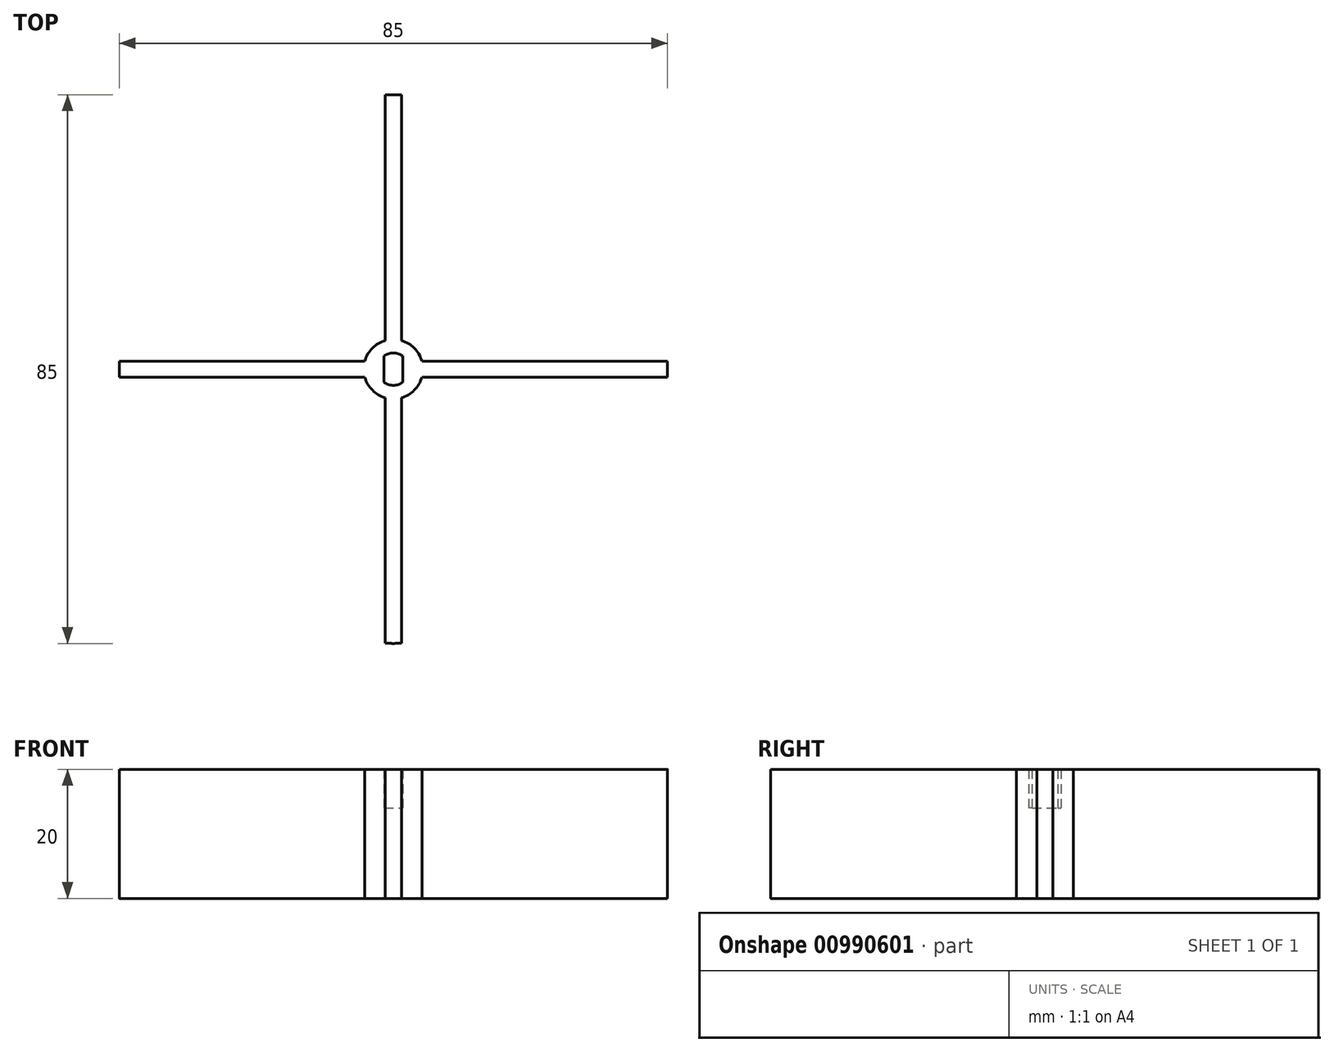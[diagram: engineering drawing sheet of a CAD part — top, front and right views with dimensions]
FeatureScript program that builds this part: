
annotation { "Feature Type Name" : "Feature", "Feature Type Description" : "" }
export const myFeature = defineFeature(function(context is Context, id is Id, definition is map)
    precondition{}
    {
        {
            var Q0;
            Q0=qCreatedBy(makeId("Top.planeOp"),FACE);
            var sketch = newSketch(context, id + "F0", { "sketchPlane" : qUnion([Q0])});
            skCircle(sketch, "E0", {"center": v(0, 0) * mm, "radius": 2.5 * mm});
            skSolve(sketch);
        }
        {
            var Q0;
            Q0 = qSketchRegion(id + "F0", true);
            extrude(context, id + "F1", {"entities" : qUnion([Q0]), "depth" : 8 * mm, "offsetDistance" : 25 * mm});
        }
        {
            var Q0;
            Q0=makeQuery(id+"F1.opExtrude","CAP_FACE",FACE,{"disambiguationData":[OSD([sQuery(id+"F0.wireOp",EDGE,"E0")])],"isStart":true});
            var sketch = newSketch(context, id + "F2", { "sketchPlane" : qUnion([Q0])});
            skLineSegment(sketch, "E1", {"start": v(-1.47, 2.02) * mm, "end": v(-1.48, -2.02) * mm});
            skLineSegment(sketch, "E2", {"start": v(1.48, 2.02) * mm, "end": v(1.47, -2.02) * mm});
            skLineSegment(sketch, "E3", {"start": v(-1.48, 0) * mm, "end": v(1.48, 0) * mm, "construction": true});
            skArc(sketch, "E4.0", {"start": v(-1.47, 2.02) * mm, "mid": v(-2.5, 0) * mm, "end": v(-1.47, -2.02) * mm});
            skArc(sketch, "E5.trimOffspring", {"start": v(1.47, -2.02) * mm, "mid": v(2.5, 0) * mm, "end": v(1.47, 2.02) * mm});
            skSolve(sketch);
        }
        {
            var Q0;
            Q0 = qSketchRegion(id + "F2", true);
            extrude(context, id + "F3", {"entities" : qUnion([Q0]), "operationType" : NewBodyOperationType.REMOVE, "oppositeDirection" : true, "depth" : 6 * mm, "offsetDistance" : 25 * mm});
        }
        {
            var Q0;
            Q0=makeQuery(id+"F1.opExtrude","CAP_FACE",FACE,{"disambiguationData":[OSD([sQuery(id+"F0.wireOp",EDGE,"E0")])],"isStart":false});
            var sketch = newSketch(context, id + "F4", { "sketchPlane" : qUnion([Q0])});
            skCircle(sketch, "E6", {"center": v(0, 0) * mm, "radius": 4.6 * mm});
            skSolve(sketch);
        }
        {
            var Q0;
            Q0=makeQuery(id+"F4.imprint","IMPRINT",FACE,{"disambiguationData":[TD([[makeQuery(id+"F4.imprint","IMPRINT",EDGE,{"derivedFrom":sQuery(id+"F4.wireOp",EDGE,"E6")}),1.0]])]});
            var Q1;
            Q1=makeQuery(id+"F4.imprint","IMPRINT",FACE,{"disambiguationData":[TD([[makeQuery(id+"F4.imprint","IMPRINT",EDGE,{"derivedFrom":makeQuery(id+"F1.opExtrude","CAP_EDGE",EDGE,{"disambiguationData":[OSD([sQuery(id+"F0.wireOp",EDGE,"E0")])],"isStart":false})}),1.0]])]});
            extrude(context, id + "F5", {"entities" : qUnion([Q0, Q1]), "operationType" : NewBodyOperationType.ADD, "depth" : 1.5 * mm, "offsetDistance" : 25 * mm});
        }
        {
            var Q0;
            Q0=makeQuery(id+"F5.opExtrude","CAP_FACE",FACE,{"disambiguationData":[OSD([sQuery(id+"F4.wireOp",EDGE,"E6")])],"isStart":false});
            var sketch = newSketch(context, id + "F6", { "sketchPlane" : qUnion([Q0])});
            skCircle(sketch, "E7", {"center": v(0, 7.6) * mm, "radius": 14 * mm});
            skLineSegment(sketch, "E8", {"start": v(0, 0) * mm, "end": v(0, 7.6) * mm, "construction": true});
            skSolve(sketch);
        }
        {
            var Q0;
            Q0 = qSketchRegion(id + "F6", true);
            extrude(context, id + "F7", {"entities" : qUnion([Q0]), "operationType" : NewBodyOperationType.ADD, "depth" : 19.2 * mm, "offsetDistance" : 25 * mm});
        }
        {
            var Q0;
            Q0=makeQuery(id+"F7.opExtrude","CAP_FACE",FACE,{"disambiguationData":[OSD([sQuery(id+"F6.wireOp",EDGE,"E7")])],"isStart":true});
            var sketch = newSketch(context, id + "F8", { "sketchPlane" : qUnion([Q0])});
            skLineSegment(sketch, "E9", {"start": v(-7.25, -19.58) * mm, "end": v(-7.25, -24.08) * mm});
            skLineSegment(sketch, "E10", {"start": v(-7.25, -24.08) * mm, "end": v(7.25, -24.08) * mm});
            skLineSegment(sketch, "E11", {"start": v(7.25, -24.08) * mm, "end": v(7.25, -19.58) * mm});
            skLineSegment(sketch, "E12", {"start": v(0, 0) * mm, "end": v(0, -24.08) * mm, "construction": true});
            skLineSegment(sketch, "E13", {"start": v(-7.25, -19.58) * mm, "end": v(7.25, -19.58) * mm});
            skSolve(sketch);
        }
        {
            var Q0;
            {var subQ0=sQuery(id+"F8.wireOp",EDGE,"E9");Q0=makeQuery(id+"F8.imprint","IMPRINT",FACE,{"disambiguationData":[TD([[makeQuery(id+"F8.imprint","IMPRINT",EDGE,{"derivedFrom":subQ0}),1.0]])]});}
            extrude(context, id + "F9", {"entities" : qUnion([Q0]), "operationType" : NewBodyOperationType.ADD, "oppositeDirection" : true, "depth" : 16.5 * mm, "offsetDistance" : 25 * mm});
        }
        {
            var Q0;
            Q0=makeQuery(id+"F3.boolean.opBoolean","COPY",FACE,{"derivedFrom":makeQuery(id+"F3.opExtrude","CAP_FACE",FACE,{"disambiguationData":[OSD([sQuery(id+"F2.wireOp",EDGE,"E1"),sQuery(id+"F2.wireOp",EDGE,"E4.0")])],"isStart":false})});
            var sketch = newSketch(context, id + "F10", { "sketchPlane" : qUnion([Q0])});
            skArc(sketch, "E14", {"start": v(-1.25, -42.48) * mm, "mid": v(0, -42.5) * mm, "end": v(1.25, -42.48) * mm});
            skArc(sketch, "E15", {"start": v(-4.43, -1.25) * mm, "mid": v(-3.25, -3.25) * mm, "end": v(-1.25, -4.43) * mm});
            skLineSegment(sketch, "E16", {"start": v(1.25, 42.48) * mm, "end": v(1.25, 4.43) * mm});
            skLineSegment(sketch, "E17", {"start": v(0, 42.5) * mm, "end": v(0, -42.5) * mm, "construction": true});
            skLineSegment(sketch, "E18", {"start": v(42.5, 0) * mm, "end": v(-42.5, 0) * mm, "construction": true});
            skLineSegment(sketch, "E19", {"start": v(4.43, 1.25) * mm, "end": v(42.48, 1.25) * mm});
            skLineSegment(sketch, "E20", {"start": v(4.43, -1.25) * mm, "end": v(42.48, -1.25) * mm});
            skLineSegment(sketch, "E21", {"start": v(1.25, -4.43) * mm, "end": v(1.25, -42.48) * mm});
            skLineSegment(sketch, "E22.MirrorCS", {"start": v(-1.25, 42.48) * mm, "end": v(-1.25, 4.43) * mm});
            skLineSegment(sketch, "E23.MirrorCS", {"start": v(-4.43, 1.25) * mm, "end": v(-42.48, 1.25) * mm});
            skLineSegment(sketch, "E24.MirrorCS", {"start": v(-4.43, -1.25) * mm, "end": v(-42.48, -1.25) * mm});
            skLineSegment(sketch, "E25.MirrorCS", {"start": v(-1.25, -4.43) * mm, "end": v(-1.25, -42.48) * mm});
            skArc(sketch, "E26.trimOffspring", {"start": v(4.43, 1.25) * mm, "mid": v(3.25, 3.25) * mm, "end": v(1.25, 4.43) * mm});
            skArc(sketch, "E27.trimOffspring", {"start": v(-1.25, 4.43) * mm, "mid": v(-3.25, 3.25) * mm, "end": v(-4.43, 1.25) * mm});
            skArc(sketch, "E28.trimOffspring", {"start": v(1.25, -4.43) * mm, "mid": v(3.25, -3.25) * mm, "end": v(4.43, -1.25) * mm});
            skArc(sketch, "E29.trimOffspring", {"start": v(-42.48, 1.25) * mm, "mid": v(-42.5, 0) * mm, "end": v(-42.48, -1.25) * mm});
            skArc(sketch, "E30.trimOffspring", {"start": v(1.25, 42.48) * mm, "mid": v(0, 42.5) * mm, "end": v(-1.25, 42.48) * mm});
            skArc(sketch, "E31.trimOffspring", {"start": v(42.48, -1.25) * mm, "mid": v(42.5, 0) * mm, "end": v(42.48, 1.25) * mm});
            skSolve(sketch);
        }
        {
            var Q0;
            Q0 = qSketchRegion(id + "F10", true);
            extrude(context, id + "F11", {"entities" : qUnion([Q0]), "depth" : 20 * mm, "offsetDistance" : 25 * mm});
        }
        {
            var Q0;
            Q0=makeQuery(id+"F1.opExtrude","SWEPT_BODY",BODY,{"disambiguationData":[OSD([sQuery(id+"F0.wireOp",EDGE,"E0")])]});
            var Q1;
            Q1=makeQuery(id+"F11.opExtrude","SWEPT_BODY",BODY,{"disambiguationData":[OSD([sQuery(id+"F10.wireOp",EDGE,"E14"),sQuery(id+"F10.wireOp",EDGE,"E15"),sQuery(id+"F10.wireOp",EDGE,"E16"),sQuery(id+"F10.wireOp",EDGE,"E19"),sQuery(id+"F10.wireOp",EDGE,"E20"),sQuery(id+"F10.wireOp",EDGE,"E21"),sQuery(id+"F10.wireOp",EDGE,"E22.MirrorCS"),sQuery(id+"F10.wireOp",EDGE,"E23.MirrorCS"),sQuery(id+"F10.wireOp",EDGE,"E24.MirrorCS"),sQuery(id+"F10.wireOp",EDGE,"E25.MirrorCS"),sQuery(id+"F10.wireOp",EDGE,"E26.trimOffspring"),sQuery(id+"F10.wireOp",EDGE,"E27.trimOffspring"),sQuery(id+"F10.wireOp",EDGE,"E28.trimOffspring"),sQuery(id+"F10.wireOp",EDGE,"E29.trimOffspring"),sQuery(id+"F10.wireOp",EDGE,"E30.trimOffspring"),sQuery(id+"F10.wireOp",EDGE,"E31.trimOffspring")])]});
            booleanBodies(context, id + "F12", {"operationType" : BooleanOperationType.SUBTRACTION, "tools" : qUnion([Q0]), "targets" : qUnion([Q1])});
        }
    });
